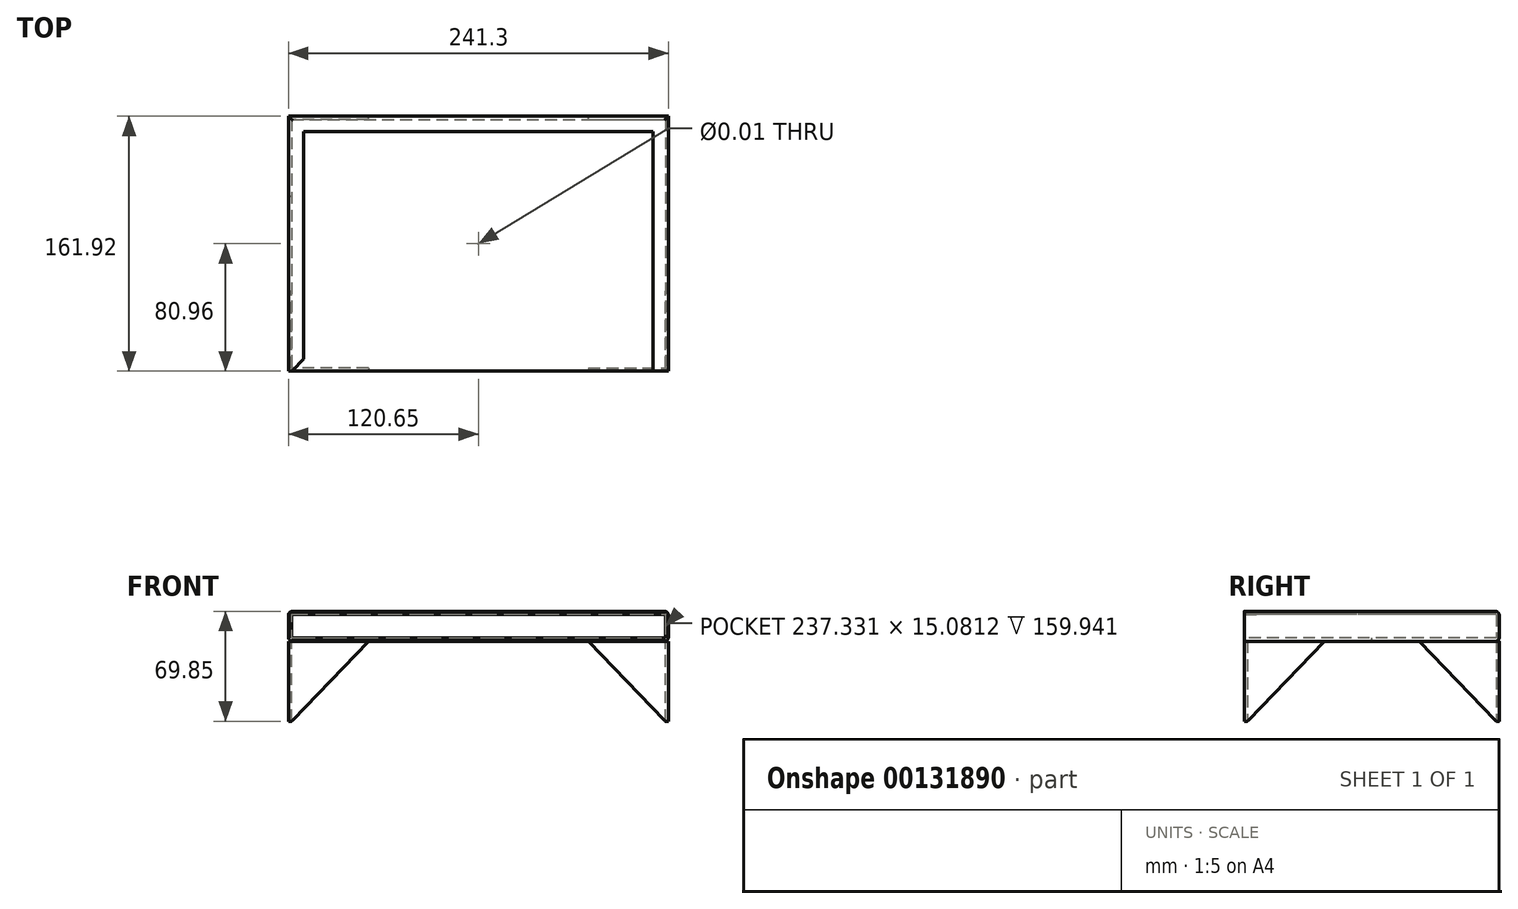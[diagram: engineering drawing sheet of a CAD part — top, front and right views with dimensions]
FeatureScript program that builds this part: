
annotation { "Feature Type Name" : "Feature", "Feature Type Description" : "" }
export const myFeature = defineFeature(function(context is Context, id is Id, definition is map)
    precondition{}
    {
        {
            var Q0;
            Q0=qCreatedBy(makeId("Top.planeOp"),FACE);
            var sketch = newSketch(context, id + "F0", { "sketchPlane" : qUnion([Q0])});
            skLineSegment(sketch, "E0.bottom", {"start": v(-120.65, 80.96) * mm, "end": v(120.65, 80.96) * mm});
            skLineSegment(sketch, "E0.top", {"start": v(-120.65, -80.96) * mm, "end": v(120.65, -80.96) * mm});
            skLineSegment(sketch, "E0.left", {"start": v(-120.65, 80.96) * mm, "end": v(-120.65, -80.96) * mm});
            skLineSegment(sketch, "E0.right", {"start": v(120.65, 80.96) * mm, "end": v(120.65, -80.96) * mm});
            skPoint(sketch, "E0.middle", {"position": v(0, 0) * mm});
            skSolve(sketch);
        }
        {
            var Q0;
            Q0=makeQuery(id+"F0.imprint","IMPRINT",FACE,{"disambiguationData":[TD([[makeQuery(id+"F0.imprint","IMPRINT",EDGE,{"derivedFrom":sQuery(id+"F0.wireOp",EDGE,"E0.bottom")}),-1.0]])]});
            extrude(context, id + "F1", {"entities" : qUnion([Q0]), "depth" : 19.05 * mm});
        }
        {
            var Q0;
            Q0=makeQuery(id+"F1.opExtrude","CAP_FACE",FACE,{"disambiguationData":[OSD([sQuery(id+"F0.wireOp",EDGE,"E0.bottom"),sQuery(id+"F0.wireOp",EDGE,"E0.top"),sQuery(id+"F0.wireOp",EDGE,"E0.left"),sQuery(id+"F0.wireOp",EDGE,"E0.right")])],"isStart":false});
            var sketch = newSketch(context, id + "F2", { "sketchPlane" : qUnion([Q0])});
            skSolve(sketch);
        }
        {
            var Q0;
            Q0=makeQuery(id+"F1.opExtrude","SWEPT_FACE",FACE,{"disambiguationData":[OSD([sQuery(id+"F0.wireOp",EDGE,"E0.top")])]});
            shell(context, id + "F3", {"entities" : qUnion([Q0]), "thickness" : 1.98 * mm});
        }
        {
            var Q0;
            Q0=makeQuery(id+"F2.imprint","IMPRINT",FACE,{"disambiguationData":[TD([[makeQuery(id+"F2.imprint","IMPRINT",EDGE,{"derivedFrom":makeQuery(id+"F1.opExtrude","CAP_EDGE",EDGE,{"disambiguationData":[OSD([sQuery(id+"F0.wireOp",EDGE,"E0.bottom")])],"isStart":false})}),-1.0]])]});
            var sketch = newSketch(context, id + "F4", { "sketchPlane" : qUnion([Q0])});
            skLineSegment(sketch, "E1.bottom", {"start": v(111, 71.14) * mm, "end": v(-111, 71.14) * mm});
            skLineSegment(sketch, "E1.top", {"start": v(111, -81.27) * mm, "end": v(-111, -81.27) * mm});
            skLineSegment(sketch, "E1.left", {"start": v(111, 71.14) * mm, "end": v(111, -81.27) * mm});
            skLineSegment(sketch, "E1.right", {"start": v(-111, 71.14) * mm, "end": v(-111, -81.27) * mm});
            skPoint(sketch, "E1.middle", {"position": v(0, -5.06) * mm});
            skSolve(sketch);
        }
        {
            var Q0;
            Q0 = qSketchRegion(id + "F4", true);
            extrude(context, id + "F5", {"entities" : qUnion([Q0]), "operationType" : NewBodyOperationType.REMOVE, "oppositeDirection" : true, "depth" : 5.18 * mm});
        }
        {
            var Q0;
            Q0=makeQuery(id+"F1.opExtrude","CAP_FACE",FACE,{"disambiguationData":[OSD([sQuery(id+"F0.wireOp",EDGE,"E0.bottom"),sQuery(id+"F0.wireOp",EDGE,"E0.top"),sQuery(id+"F0.wireOp",EDGE,"E0.left"),sQuery(id+"F0.wireOp",EDGE,"E0.right")])],"isStart":true});
            var sketch = newSketch(context, id + "F6", { "sketchPlane" : qUnion([Q0])});
            skLineSegment(sketch, "E2", {"start": v(-69.85, -80.96) * mm, "end": v(-120.65, -80.96) * mm});
            skLineSegment(sketch, "E3", {"start": v(-120.65, -80.96) * mm, "end": v(-120.65, -30.16) * mm});
            skLineSegment(sketch, "E4", {"start": v(-120.65, -30.16) * mm, "end": v(-118.67, -30.16) * mm});
            skLineSegment(sketch, "E5", {"start": v(-118.67, -30.16) * mm, "end": v(-118.67, -78.98) * mm});
            skLineSegment(sketch, "E6", {"start": v(-118.67, -78.98) * mm, "end": v(-69.85, -78.98) * mm});
            skLineSegment(sketch, "E7", {"start": v(-69.85, -78.98) * mm, "end": v(-69.85, -80.96) * mm});
            skSolve(sketch);
        }
        {
            var Q0;
            Q0 = qSketchRegion(id + "F6", true);
            extrude(context, id + "F7", {"entities" : qUnion([Q0]), "depth" : 50.8 * mm});
        }
        {
            var Q0;
            Q0=makeQuery(id+"F7.opExtrude","SWEPT_FACE",FACE,{"disambiguationData":[OSD([sQuery(id+"F6.wireOp",EDGE,"E3")])]});
            var sketch = newSketch(context, id + "F8", { "sketchPlane" : qUnion([Q0])});
            skLineSegment(sketch, "E8", {"start": v(-78.98, -50.8) * mm, "end": v(-30.16, 0) * mm});
            skLineSegment(sketch, "E9", {"start": v(-30.16, 0) * mm, "end": v(-30.16, -50.8) * mm});
            skLineSegment(sketch, "E10", {"start": v(-30.16, -50.8) * mm, "end": v(-78.98, -50.8) * mm});
            skSolve(sketch);
        }
        {
            var Q0;
            Q0 = qSketchRegion(id + "F8", true);
            extrude(context, id + "F9", {"entities" : qUnion([Q0]), "operationType" : NewBodyOperationType.REMOVE, "endBound" : BoundingType.UP_TO_NEXT, "oppositeDirection" : true, "depth" : 25.4 * mm});
        }
        {
            var Q0;
            Q0=makeQuery(id+"F7.opExtrude","SWEPT_FACE",FACE,{"disambiguationData":[OSD([sQuery(id+"F6.wireOp",EDGE,"E2")])]});
            var sketch = newSketch(context, id + "F10", { "sketchPlane" : qUnion([Q0])});
            skLineSegment(sketch, "E11", {"start": v(69.85, 0) * mm, "end": v(118.67, -50.8) * mm});
            skLineSegment(sketch, "E12", {"start": v(118.67, -50.8) * mm, "end": v(69.85, -50.8) * mm});
            skLineSegment(sketch, "E13", {"start": v(69.85, -50.8) * mm, "end": v(69.85, 0) * mm});
            skSolve(sketch);
        }
        {
            var Q0;
            Q0 = qSketchRegion(id + "F10", true);
            extrude(context, id + "F11", {"entities" : qUnion([Q0]), "operationType" : NewBodyOperationType.REMOVE, "endBound" : BoundingType.UP_TO_NEXT, "oppositeDirection" : true, "depth" : 25.4 * mm});
        }
        {
            var Q0;
            Q0=makeQuery(id+"F7.opExtrude","SWEPT_BODY",BODY,{"disambiguationData":[OSD([sQuery(id+"F6.wireOp",EDGE,"E2"),sQuery(id+"F6.wireOp",EDGE,"E3"),sQuery(id+"F6.wireOp",EDGE,"E4"),sQuery(id+"F6.wireOp",EDGE,"E5"),sQuery(id+"F6.wireOp",EDGE,"E6"),sQuery(id+"F6.wireOp",EDGE,"E7")])]});
            var Q1;
            Q1=qCreatedBy(makeId("Right.planeOp"),FACE);
            mirror(context, id + "F12", {"entities" : qUnion([Q0]), "mirrorPlane" : qUnion([Q1])});
        }
        {
            var Q0;
            Q0=makeQuery(id+"F12.opPattern","COPY",BODY,{"derivedFrom":makeQuery(id+"F7.opExtrude","SWEPT_BODY",BODY,{"disambiguationData":[OSD([sQuery(id+"F6.wireOp",EDGE,"E2"),sQuery(id+"F6.wireOp",EDGE,"E3"),sQuery(id+"F6.wireOp",EDGE,"E4"),sQuery(id+"F6.wireOp",EDGE,"E5"),sQuery(id+"F6.wireOp",EDGE,"E6"),sQuery(id+"F6.wireOp",EDGE,"E7")])]}),"instanceName":"1"});
            var Q1;
            Q1=makeQuery(id+"F7.opExtrude","SWEPT_BODY",BODY,{"disambiguationData":[OSD([sQuery(id+"F6.wireOp",EDGE,"E2"),sQuery(id+"F6.wireOp",EDGE,"E3"),sQuery(id+"F6.wireOp",EDGE,"E4"),sQuery(id+"F6.wireOp",EDGE,"E5"),sQuery(id+"F6.wireOp",EDGE,"E6"),sQuery(id+"F6.wireOp",EDGE,"E7")])]});
            var Q2;
            Q2=qCreatedBy(makeId("Front.planeOp"),FACE);
            mirror(context, id + "F13", {"entities" : qUnion([Q0, Q1]), "mirrorPlane" : qUnion([Q2])});
        }
        {
            var Q0;
            Q0=makeQuery(id+"F1.opExtrude","CAP_EDGE",EDGE,{"disambiguationData":[OSD([sQuery(id+"F0.wireOp",EDGE,"E0.left")])],"isStart":false});
            var Q1;
            Q1=makeQuery(id+"F1.opExtrude","CAP_EDGE",EDGE,{"disambiguationData":[OSD([sQuery(id+"F0.wireOp",EDGE,"E0.bottom")])],"isStart":false});
            var Q2;
            Q2=makeQuery(id+"F1.opExtrude","CAP_EDGE",EDGE,{"disambiguationData":[OSD([sQuery(id+"F0.wireOp",EDGE,"E0.right")])],"isStart":false});
            var Q3;
            Q3=makeQuery(id+"F1.opExtrude","CAP_EDGE",EDGE,{"disambiguationData":[OSD([sQuery(id+"F0.wireOp",EDGE,"E0.left")])],"isStart":true});
            var Q4;
            Q4=makeQuery(id+"F1.opExtrude","CAP_EDGE",EDGE,{"disambiguationData":[OSD([sQuery(id+"F0.wireOp",EDGE,"E0.bottom")])],"isStart":true});
            var Q5;
            Q5=makeQuery(id+"F1.opExtrude","CAP_EDGE",EDGE,{"disambiguationData":[OSD([sQuery(id+"F0.wireOp",EDGE,"E0.right")])],"isStart":true});
            fillet(context, id + "F14", {"entities" : qUnion([Q0, Q1, Q2, Q3, Q4, Q5]), "radius" : 2.54 * mm, "tangentPropagation" : true, "allowEdgeOverflow" : false});
        }
        {
            var Q0;
            Q0=makeQuery(id+"F7.opExtrude","SWEPT_EDGE",EDGE,{"disambiguationData":[OSD([sQuery(id+"F6.wireOp",EDGE,"E2"),sQuery(id+"F6.wireOp",EDGE,"E3")])]});
            var Q1;
            Q1=makeQuery(id+"F13.opPattern","COPY",EDGE,{"derivedFrom":makeQuery(id+"F7.opExtrude","SWEPT_EDGE",EDGE,{"disambiguationData":[OSD([sQuery(id+"F6.wireOp",EDGE,"E2"),sQuery(id+"F6.wireOp",EDGE,"E3")])]}),"instanceName":"1"});
            var Q2;
            Q2=makeQuery(id+"F13.opPattern","COPY",EDGE,{"derivedFrom":makeQuery(id+"F12.opPattern","COPY",EDGE,{"derivedFrom":makeQuery(id+"F7.opExtrude","SWEPT_EDGE",EDGE,{"disambiguationData":[OSD([sQuery(id+"F6.wireOp",EDGE,"E2"),sQuery(id+"F6.wireOp",EDGE,"E3")])]}),"instanceName":"1"}),"instanceName":"1"});
            var Q3;
            Q3=makeQuery(id+"F12.opPattern","COPY",EDGE,{"derivedFrom":makeQuery(id+"F7.opExtrude","SWEPT_EDGE",EDGE,{"disambiguationData":[OSD([sQuery(id+"F6.wireOp",EDGE,"E2"),sQuery(id+"F6.wireOp",EDGE,"E3")])]}),"instanceName":"1"});
            fillet(context, id + "F15", {"entities" : qUnion([Q0, Q1, Q2, Q3]), "radius" : 2.54 * mm, "tangentPropagation" : true, "allowEdgeOverflow" : false});
        }
        {
            var Q0;
            {var subQ0=sQuery(id+"F0.wireOp",EDGE,"E0.right");var subQ1=sQuery(id+"F0.wireOp",EDGE,"E0.left");var subQ2=sQuery(id+"F0.wireOp",EDGE,"E0.top");var subQ3=sQuery(id+"F0.wireOp",EDGE,"E0.bottom");Q0=makeQuery(id+"F3.opShell","OFFSET_FACE",FACE,{"disambiguationData":[OSD([subQ3,subQ2,subQ1,subQ0]),TDD([makeQuery(id+"F1.opExtrude","CAP_FACE",FACE,{"disambiguationData":[OSD([subQ3,subQ2,subQ1,subQ0])],"isStart":false})])]});}
            var sketch = newSketch(context, id + "F16", { "sketchPlane" : qUnion([Q0])});
            skLineSegment(sketch, "E14", {"start": v(-111, 80.96) * mm, "end": v(-118.67, 80.96) * mm});
            skLineSegment(sketch, "E15", {"start": v(-118.67, 80.96) * mm, "end": v(-111, 73.29) * mm});
            skLineSegment(sketch, "E16", {"start": v(-111, 73.29) * mm, "end": v(-111, 80.96) * mm});
            skSolve(sketch);
        }
        {
            var Q0;
            Q0 = qSketchRegion(id + "F16", true);
            extrude(context, id + "F17", {"entities" : qUnion([Q0]), "operationType" : NewBodyOperationType.REMOVE, "endBound" : BoundingType.UP_TO_NEXT, "oppositeDirection" : true, "depth" : 5.5 * mm});
        }
        {
            var Q0;
            Q0=makeQuery(id+"F2.imprint","IMPRINT",FACE,{"disambiguationData":[TD([[makeQuery(id+"F2.imprint","IMPRINT",EDGE,{"derivedFrom":makeQuery(id+"F1.opExtrude","CAP_EDGE",EDGE,{"disambiguationData":[OSD([sQuery(id+"F0.wireOp",EDGE,"E0.bottom")])],"isStart":false})}),-1.0]])]});
            var sketch = newSketch(context, id + "F18", { "sketchPlane" : qUnion([Q0])});
            skPoint(sketch, "E17", {"position": v(0, 0) * mm});
            skSolve(sketch);
        }
        {
            var Q0;
            Q0=sQuery(id+"F18.wireOp",VERTEX,"E17");
            var Q1;
            Q1=makeQuery(id+"F1.opExtrude","SWEPT_BODY",BODY,{"disambiguationData":[OSD([sQuery(id+"F0.wireOp",EDGE,"E0.bottom"),sQuery(id+"F0.wireOp",EDGE,"E0.top"),sQuery(id+"F0.wireOp",EDGE,"E0.left"),sQuery(id+"F0.wireOp",EDGE,"E0.right")])]});
            hole(context, id + "F19", {"style" : HoleStyle.SIMPLE, "endStyle" : HoleEndStyle.THROUGH, "standardTappedOrClearance" : lookupTablePath({ "standard" : "ANSI", "size" : "3/8 (0.38)", "type" : "Drilled" }), "standardBlindInLast" : lookupTablePath({ "standard" : "ANSI", "size" : "3/8", "type" : "Drilled" }), "holeDiameter" : 3 / 203.2 * mm, "locations" : qUnion([Q0]), "scope" : qUnion([Q1]), "isTappedThrough" : true});
        }
    });
